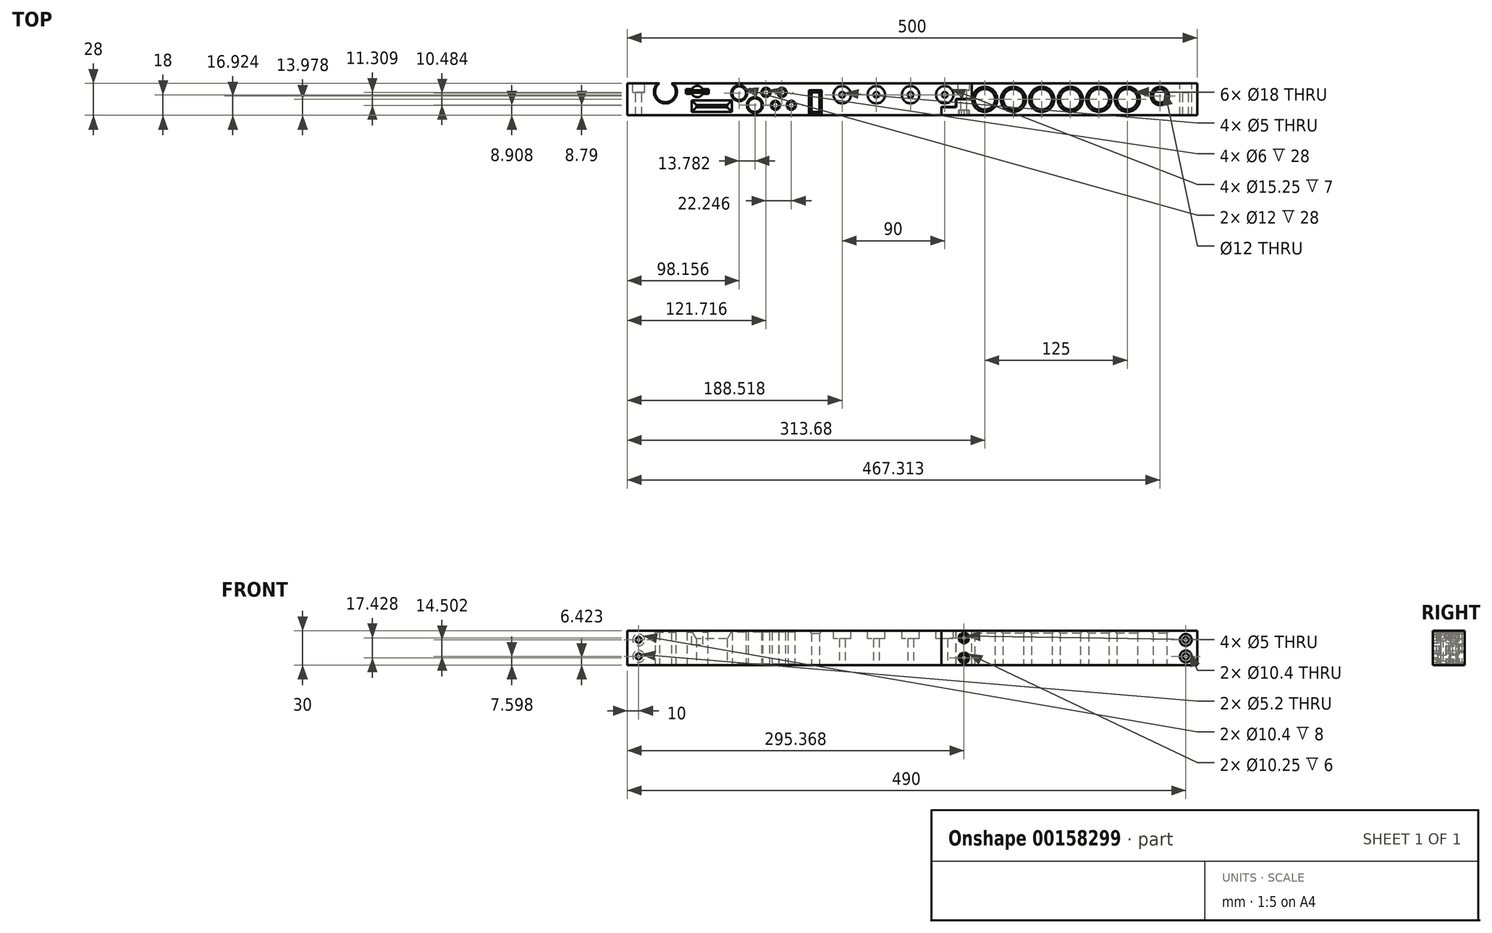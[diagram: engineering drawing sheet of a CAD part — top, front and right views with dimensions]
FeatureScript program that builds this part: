
annotation { "Feature Type Name" : "Feature", "Feature Type Description" : "" }
export const myFeature = defineFeature(function(context is Context, id is Id, definition is map)
    precondition{}
    {
        {
            var Q0;
            Q0=qCreatedBy(makeId("Top.planeOp"),FACE);
            var sketch = newSketch(context, id + "F0", { "sketchPlane" : qUnion([Q0])});
            skLineSegment(sketch, "E0.bottom", {"start": v(0, 0) * mm, "end": v(-211.32, 0) * mm});
            skLineSegment(sketch, "E0.top", {"start": v(0, -28) * mm, "end": v(-250, -28) * mm});
            skLineSegment(sketch, "E0.right", {"start": v(-250, 0) * mm, "end": v(-250, -28) * mm});
            skLineSegment(sketch, "E1.MirrorCS", {"start": v(0, 0) * mm, "end": v(250, 0) * mm});
            skLineSegment(sketch, "E2.MirrorCS", {"start": v(250, 0) * mm, "end": v(250, -28) * mm});
            skLineSegment(sketch, "E3.MirrorCS", {"start": v(0, -28) * mm, "end": v(250, -28) * mm});
            skArc(sketch, "E4", {"start": v(-221.74, 0) * mm, "mid": v(-216.53, -16.56) * mm, "end": v(-211.32, 0) * mm});
            skPoint(sketch, "E5", {"position": v(-211.32, 0) * mm});
            skPoint(sketch, "E6", {"position": v(-221.74, 0) * mm});
            skLineSegment(sketch, "E7.trimOffspring", {"start": v(-221.74, 0) * mm, "end": v(-250, 0) * mm});
            skLineSegment(sketch, "E8.bottom", {"start": v(-189.32, -19) * mm, "end": v(-162.32, -19) * mm});
            skLineSegment(sketch, "E8.top", {"start": v(-189.32, -21) * mm, "end": v(-162.32, -21) * mm});
            skLineSegment(sketch, "E8.left", {"start": v(-189.32, -19) * mm, "end": v(-189.32, -21) * mm});
            skLineSegment(sketch, "E8.right", {"start": v(-162.32, -19) * mm, "end": v(-162.32, -21) * mm});
            skLineSegment(sketch, "E9.bottom", {"start": v(-197.6, -6.14) * mm, "end": v(-179.6, -6.14) * mm});
            skLineSegment(sketch, "E9.top", {"start": v(-197.6, -8.14) * mm, "end": v(-179.6, -8.14) * mm});
            skLineSegment(sketch, "E9.left", {"start": v(-197.6, -6.14) * mm, "end": v(-197.6, -8.14) * mm});
            skLineSegment(sketch, "E9.right", {"start": v(-179.6, -6.14) * mm, "end": v(-179.6, -8.14) * mm});
            skLineSegment(sketch, "E10", {"start": v(-197.6, -7.14) * mm, "end": v(-179.6, -7.14) * mm, "construction": true});
            skLineSegment(sketch, "E11", {"start": v(-188.6, -6.14) * mm, "end": v(-188.6, -8.14) * mm, "construction": true});
            skCircle(sketch, "E12", {"center": v(-151.84, -8.6) * mm, "radius": 6 * mm});
            skCircle(sketch, "E13", {"center": v(-138.06, -19.1) * mm, "radius": 6 * mm});
            skCircle(sketch, "E14", {"center": v(-128.28, -7.9) * mm, "radius": 3 * mm});
            skCircle(sketch, "E15", {"center": v(-120.04, -19.21) * mm, "radius": 3 * mm});
            skCircle(sketch, "E16", {"center": v(-114.28, -7.9) * mm, "radius": 3 * mm});
            skCircle(sketch, "E17", {"center": v(-106.04, -19.21) * mm, "radius": 3 * mm});
            skLineSegment(sketch, "E18", {"start": v(-94.24, -10) * mm, "end": v(-13.08, -10) * mm, "construction": true});
            skCircle(sketch, "E19", {"center": v(-61.48, -10) * mm, "radius": 2.5 * mm});
            skCircle(sketch, "E20.1.0.0", {"center": v(-31.48, -10) * mm, "radius": 2.5 * mm});
            skCircle(sketch, "E20.2.0.0", {"center": v(-1.48, -10) * mm, "radius": 2.5 * mm});
            skCircle(sketch, "E20.3.0.0", {"center": v(28.52, -10) * mm, "radius": 2.5 * mm});
            skLineSegment(sketch, "E20.direction1", {"start": v(-61.48, -10) * mm, "end": v(-31.48, -10) * mm, "construction": true});
            skLineSegment(sketch, "E21.bottom", {"start": v(-81.48, -25) * mm, "end": v(-88.48, -25) * mm});
            skLineSegment(sketch, "E21.top", {"start": v(-81.48, -8) * mm, "end": v(-88.48, -8) * mm});
            skLineSegment(sketch, "E21.left", {"start": v(-81.48, -25) * mm, "end": v(-81.48, -8) * mm});
            skLineSegment(sketch, "E21.right", {"start": v(-88.48, -25) * mm, "end": v(-88.48, -8) * mm});
            skLineSegment(sketch, "E22.bottom", {"start": v(-61.48, -10) * mm, "end": v(-60.58, -10) * mm});
            skLineSegment(sketch, "E22.top", {"start": v(-61.48, -10) * mm, "end": v(-60.58, -10) * mm});
            skLineSegment(sketch, "E22.left", {"start": v(-61.48, -10) * mm, "end": v(-61.48, -10) * mm});
            skLineSegment(sketch, "E22.right", {"start": v(-60.58, -10) * mm, "end": v(-60.58, -10) * mm});
            skCircle(sketch, "E23", {"center": v(63.68, -14.02) * mm, "radius": 9 * mm});
            skCircle(sketch, "E24.1.0.0", {"center": v(88.68, -14.02) * mm, "radius": 9 * mm});
            skCircle(sketch, "E24.2.0.0", {"center": v(113.68, -14.02) * mm, "radius": 9 * mm});
            skCircle(sketch, "E24.3.0.0", {"center": v(138.68, -14.02) * mm, "radius": 9 * mm});
            skCircle(sketch, "E24.4.0.0", {"center": v(163.68, -14.02) * mm, "radius": 9 * mm});
            skCircle(sketch, "E24.5.0.0", {"center": v(188.68, -14.02) * mm, "radius": 9 * mm});
            skLineSegment(sketch, "E24.direction1", {"start": v(63.68, -14.02) * mm, "end": v(88.68, -14.02) * mm, "construction": true});
            skLineSegment(sketch, "E25.bottom", {"start": v(250, -6.13) * mm, "end": v(230, -6.13) * mm, "construction": true});
            skLineSegment(sketch, "E25.top", {"start": v(250, -18.38) * mm, "end": v(230, -18.38) * mm, "construction": true});
            skLineSegment(sketch, "E25.left", {"start": v(250, -6.13) * mm, "end": v(250, -18.38) * mm, "construction": true});
            skLineSegment(sketch, "E25.right", {"start": v(230, -6.13) * mm, "end": v(230, -18.38) * mm, "construction": true});
            skCircle(sketch, "E26", {"center": v(217.31, -11.08) * mm, "radius": 6 * mm});
            skSolve(sketch);
        }
        {
            var Q0;
            Q0 = qSketchRegion(id + "F0", true);
            extrude(context, id + "F1", {"entities" : qUnion([Q0]), "depth" : 30 * mm, "offsetDistance" : 25 * mm});
        }
        {
            var Q0;
            Q0=makeQuery(id+"F1.opExtrude","SWEPT_FACE",FACE,{"disambiguationData":[OSD([sQuery(id+"F0.wireOp",EDGE,"E0.bottom"),sQuery(id+"F0.wireOp",EDGE,"E1.MirrorCS")])]});
            var sketch = newSketch(context, id + "F2", { "sketchPlane" : qUnion([Q0])});
            skLineSegment(sketch, "E27", {"start": v(240, 30) * mm, "end": v(240, 0) * mm, "construction": true});
            skCircle(sketch, "E28", {"center": v(240, 22.1) * mm, "radius": 2.6 * mm});
            skCircle(sketch, "E29", {"center": v(240, 7.6) * mm, "radius": 2.6 * mm});
            skCircle(sketch, "E30", {"center": v(240, 22.1) * mm, "radius": 5.2 * mm});
            skCircle(sketch, "E31", {"center": v(240, 7.6) * mm, "radius": 5.2 * mm});
            skCircle(sketch, "E32.MirrorC", {"center": v(-240, 7.6) * mm, "radius": 2.6 * mm});
            skCircle(sketch, "E33.MirrorC", {"center": v(-240, 22.1) * mm, "radius": 2.6 * mm});
            skCircle(sketch, "E34.MirrorC", {"center": v(-240, 22.1) * mm, "radius": 5.2 * mm});
            skCircle(sketch, "E35.MirrorC", {"center": v(-240, 7.6) * mm, "radius": 5.2 * mm});
            skSolve(sketch);
        }
        {
            var Q0;
            Q0=makeQuery(id+"F2.imprint","IMPRINT",FACE,{"disambiguationData":[TD([[makeQuery(id+"F2.imprint","IMPRINT",EDGE,{"derivedFrom":sQuery(id+"F2.wireOp",EDGE,"E28")}),1.0]])]});
            var Q1;
            Q1=makeQuery(id+"F2.imprint","IMPRINT",FACE,{"disambiguationData":[TD([[makeQuery(id+"F2.imprint","IMPRINT",EDGE,{"derivedFrom":sQuery(id+"F2.wireOp",EDGE,"E29")}),1.0]])]});
            var Q2;
            Q2=makeQuery(id+"F2.imprint","IMPRINT",FACE,{"disambiguationData":[TD([[makeQuery(id+"F2.imprint","IMPRINT",EDGE,{"derivedFrom":sQuery(id+"F2.wireOp",EDGE,"E32.MirrorC")}),-1.0]])]});
            var Q3;
            Q3=makeQuery(id+"F2.imprint","IMPRINT",FACE,{"disambiguationData":[TD([[makeQuery(id+"F2.imprint","IMPRINT",EDGE,{"derivedFrom":sQuery(id+"F2.wireOp",EDGE,"E33.MirrorC")}),-1.0]])]});
            extrude(context, id + "F3", {"entities" : qUnion([Q0, Q1, Q2, Q3]), "operationType" : NewBodyOperationType.REMOVE, "endBound" : BoundingType.THROUGH_ALL, "oppositeDirection" : true, "depth" : 25 * mm, "offsetDistance" : 25 * mm});
        }
        {
            var Q0;
            Q0=makeQuery(id+"F2.imprint","IMPRINT",FACE,{"disambiguationData":[TD([[makeQuery(id+"F2.imprint","IMPRINT",EDGE,{"derivedFrom":sQuery(id+"F2.wireOp",EDGE,"E33.MirrorC")}),1.0]])]});
            var Q1;
            Q1=makeQuery(id+"F2.imprint","IMPRINT",FACE,{"disambiguationData":[TD([[makeQuery(id+"F2.imprint","IMPRINT",EDGE,{"derivedFrom":sQuery(id+"F2.wireOp",EDGE,"E32.MirrorC")}),1.0]])]});
            var Q2;
            Q2=makeQuery(id+"F2.imprint","IMPRINT",FACE,{"disambiguationData":[TD([[makeQuery(id+"F2.imprint","IMPRINT",EDGE,{"derivedFrom":sQuery(id+"F2.wireOp",EDGE,"E29")}),-1.0]])]});
            var Q3;
            Q3=makeQuery(id+"F2.imprint","IMPRINT",FACE,{"disambiguationData":[TD([[makeQuery(id+"F2.imprint","IMPRINT",EDGE,{"derivedFrom":sQuery(id+"F2.wireOp",EDGE,"E28")}),-1.0]])]});
            extrude(context, id + "F4", {"entities" : qUnion([Q0, Q1, Q2, Q3]), "operationType" : NewBodyOperationType.REMOVE, "oppositeDirection" : true, "depth" : 8 * mm, "offsetDistance" : 25 * mm});
        }
        {
            var Q0;
            Q0=makeQuery(id+"F1.opExtrude","CAP_FACE",FACE,{"disambiguationData":[OSD([sQuery(id+"F0.wireOp",EDGE,"E0.bottom"),sQuery(id+"F0.wireOp",EDGE,"E0.top"),sQuery(id+"F0.wireOp",EDGE,"E0.right"),sQuery(id+"F0.wireOp",EDGE,"E1.MirrorCS"),sQuery(id+"F0.wireOp",EDGE,"E2.MirrorCS"),sQuery(id+"F0.wireOp",EDGE,"E3.MirrorCS"),sQuery(id+"F0.wireOp",EDGE,"E4"),sQuery(id+"F0.wireOp",EDGE,"E7.trimOffspring"),sQuery(id+"F0.wireOp",EDGE,"E8.bottom"),sQuery(id+"F0.wireOp",EDGE,"E8.top"),sQuery(id+"F0.wireOp",EDGE,"E8.left"),sQuery(id+"F0.wireOp",EDGE,"E8.right"),sQuery(id+"F0.wireOp",EDGE,"E9.bottom"),sQuery(id+"F0.wireOp",EDGE,"E9.top"),sQuery(id+"F0.wireOp",EDGE,"E9.left"),sQuery(id+"F0.wireOp",EDGE,"E9.right"),sQuery(id+"F0.wireOp",EDGE,"E12"),sQuery(id+"F0.wireOp",EDGE,"E13"),sQuery(id+"F0.wireOp",EDGE,"E14"),sQuery(id+"F0.wireOp",EDGE,"E15"),sQuery(id+"F0.wireOp",EDGE,"E16"),sQuery(id+"F0.wireOp",EDGE,"E17"),sQuery(id+"F0.wireOp",EDGE,"E19"),sQuery(id+"F0.wireOp",EDGE,"E20.1.0.0"),sQuery(id+"F0.wireOp",EDGE,"E20.2.0.0"),sQuery(id+"F0.wireOp",EDGE,"E20.3.0.0"),sQuery(id+"F0.wireOp",EDGE,"E21.bottom"),sQuery(id+"F0.wireOp",EDGE,"E21.top"),sQuery(id+"F0.wireOp",EDGE,"E21.left"),sQuery(id+"F0.wireOp",EDGE,"E21.right"),sQuery(id+"F0.wireOp",EDGE,"E23"),sQuery(id+"F0.wireOp",EDGE,"E24.1.0.0"),sQuery(id+"F0.wireOp",EDGE,"E24.2.0.0"),sQuery(id+"F0.wireOp",EDGE,"E24.3.0.0"),sQuery(id+"F0.wireOp",EDGE,"E24.4.0.0"),sQuery(id+"F0.wireOp",EDGE,"E24.5.0.0"),sQuery(id+"F0.wireOp",EDGE,"E26")])],"isStart":false});
            var sketch = newSketch(context, id + "F5", { "sketchPlane" : qUnion([Q0])});
            skLineSegment(sketch, "E36.0", {"start": v(-188.6, -6.14) * mm, "end": v(-188.6, -8.14) * mm, "construction": true});
            skLineSegment(sketch, "E37.1", {"start": v(-197.6, -7.14) * mm, "end": v(-179.6, -7.14) * mm, "construction": true});
            skCircle(sketch, "E38", {"center": v(-188.6, -7.14) * mm, "radius": 5 * mm});
            skCircle(sketch, "E39", {"center": v(-61.48, -10) * mm, "radius": 7.62 * mm});
            skCircle(sketch, "E40", {"center": v(-31.48, -10) * mm, "radius": 7.62 * mm});
            skCircle(sketch, "E41", {"center": v(-1.48, -10) * mm, "radius": 7.62 * mm});
            skCircle(sketch, "E42", {"center": v(28.52, -10) * mm, "radius": 7.62 * mm});
            skSolve(sketch);
        }
        {
            var Q0;
            {var subQ0=sQuery(id+"F5.wireOp",EDGE,"E38");var subQ1=makeQuery(id+"F1.opExtrude","CAP_EDGE",EDGE,{"disambiguationData":[OSD([sQuery(id+"F0.wireOp",EDGE,"E9.bottom")])],"isStart":false});var subQ2=makeQuery(id+"F5.imprint","INTERSECT",VERTEX,{"disambiguationData":[OD(0.0)],"derivedFrom":[subQ1,subQ0]});Q0=makeQuery(id+"F5.imprint","IMPRINT",FACE,{"disambiguationData":[TD([[makeQuery(id+"F5.imprint","IMPRINT",EDGE,{"disambiguationData":[TD([[subQ2,1.0]])],"derivedFrom":subQ0}),1.0]])]});}
            var Q1;
            {var subQ0=sQuery(id+"F5.wireOp",EDGE,"E38");var subQ1=makeQuery(id+"F1.opExtrude","CAP_EDGE",EDGE,{"disambiguationData":[OSD([sQuery(id+"F0.wireOp",EDGE,"E9.top")])],"isStart":false});var subQ2=makeQuery(id+"F5.imprint","INTERSECT",VERTEX,{"disambiguationData":[OD(0.0)],"derivedFrom":[subQ1,subQ0]});Q1=makeQuery(id+"F5.imprint","IMPRINT",FACE,{"disambiguationData":[TD([[makeQuery(id+"F5.imprint","IMPRINT",EDGE,{"disambiguationData":[TD([[subQ2,-1.0]])],"derivedFrom":subQ0}),1.0]])]});}
            extrude(context, id + "F6", {"entities" : qUnion([Q0, Q1]), "operationType" : NewBodyOperationType.REMOVE, "oppositeDirection" : true, "depth" : 12 * mm, "offsetDistance" : 25 * mm});
        }
        {
            var Q0;
            Q0=makeQuery(id+"F5.imprint","IMPRINT",FACE,{"disambiguationData":[TD([[makeQuery(id+"F5.imprint","IMPRINT",EDGE,{"derivedFrom":sQuery(id+"F5.wireOp",EDGE,"E39")}),1.0]])]});
            var Q1;
            Q1=makeQuery(id+"F5.imprint","IMPRINT",FACE,{"disambiguationData":[TD([[makeQuery(id+"F5.imprint","IMPRINT",EDGE,{"derivedFrom":sQuery(id+"F5.wireOp",EDGE,"E40")}),1.0]])]});
            var Q2;
            Q2=makeQuery(id+"F5.imprint","IMPRINT",FACE,{"disambiguationData":[TD([[makeQuery(id+"F5.imprint","IMPRINT",EDGE,{"derivedFrom":sQuery(id+"F5.wireOp",EDGE,"E41")}),1.0]])]});
            var Q3;
            Q3=makeQuery(id+"F5.imprint","IMPRINT",FACE,{"disambiguationData":[TD([[makeQuery(id+"F5.imprint","IMPRINT",EDGE,{"derivedFrom":sQuery(id+"F5.wireOp",EDGE,"E42")}),1.0]])]});
            extrude(context, id + "F7", {"entities" : qUnion([Q0, Q1, Q2, Q3]), "operationType" : NewBodyOperationType.REMOVE, "oppositeDirection" : true, "depth" : 7 * mm, "offsetDistance" : 25 * mm});
        }
        {
            var Q0;
            Q0=makeQuery(id+"F1.opExtrude","CAP_EDGE",EDGE,{"disambiguationData":[OSD([sQuery(id+"F0.wireOp",EDGE,"E23")])],"isStart":false});
            var Q1;
            Q1=makeQuery(id+"F1.opExtrude","CAP_EDGE",EDGE,{"disambiguationData":[OSD([sQuery(id+"F0.wireOp",EDGE,"E24.1.0.0")])],"isStart":false});
            var Q2;
            Q2=makeQuery(id+"F1.opExtrude","CAP_EDGE",EDGE,{"disambiguationData":[OSD([sQuery(id+"F0.wireOp",EDGE,"E24.2.0.0")])],"isStart":false});
            var Q3;
            Q3=makeQuery(id+"F1.opExtrude","CAP_EDGE",EDGE,{"disambiguationData":[OSD([sQuery(id+"F0.wireOp",EDGE,"E24.3.0.0")])],"isStart":false});
            var Q4;
            Q4=makeQuery(id+"F1.opExtrude","CAP_EDGE",EDGE,{"disambiguationData":[OSD([sQuery(id+"F0.wireOp",EDGE,"E24.4.0.0")])],"isStart":false});
            var Q5;
            Q5=makeQuery(id+"F1.opExtrude","CAP_EDGE",EDGE,{"disambiguationData":[OSD([sQuery(id+"F0.wireOp",EDGE,"E24.5.0.0")])],"isStart":false});
            var Q6;
            Q6=makeQuery(id+"F1.opExtrude","CAP_EDGE",EDGE,{"disambiguationData":[OSD([sQuery(id+"F0.wireOp",EDGE,"E26")])],"isStart":false});
            var Q7;
            Q7=makeQuery(id+"F1.opExtrude","CAP_EDGE",EDGE,{"disambiguationData":[OSD([sQuery(id+"F0.wireOp",EDGE,"E21.left")])],"isStart":false});
            var Q8;
            Q8=makeQuery(id+"F1.opExtrude","CAP_EDGE",EDGE,{"disambiguationData":[OSD([sQuery(id+"F0.wireOp",EDGE,"E21.bottom")])],"isStart":false});
            var Q9;
            Q9=makeQuery(id+"F1.opExtrude","CAP_EDGE",EDGE,{"disambiguationData":[OSD([sQuery(id+"F0.wireOp",EDGE,"E21.right")])],"isStart":false});
            var Q10;
            Q10=makeQuery(id+"F1.opExtrude","CAP_EDGE",EDGE,{"disambiguationData":[OSD([sQuery(id+"F0.wireOp",EDGE,"E21.top")])],"isStart":false});
            chamfer(context, id + "F8", {"entities" : qUnion([Q0, Q1, Q2, Q3, Q4, Q5, Q6, Q7, Q8, Q9, Q10]), "width" : 2 * mm, "tangentPropagation" : true});
        }
        {
            var Q0;
            Q0=makeQuery(id+"F1.opExtrude","CAP_EDGE",EDGE,{"disambiguationData":[OSD([sQuery(id+"F0.wireOp",EDGE,"E17")])],"isStart":false});
            var Q1;
            Q1=makeQuery(id+"F1.opExtrude","CAP_EDGE",EDGE,{"disambiguationData":[OSD([sQuery(id+"F0.wireOp",EDGE,"E15")])],"isStart":false});
            var Q2;
            Q2=makeQuery(id+"F1.opExtrude","CAP_EDGE",EDGE,{"disambiguationData":[OSD([sQuery(id+"F0.wireOp",EDGE,"E16")])],"isStart":false});
            var Q3;
            Q3=makeQuery(id+"F1.opExtrude","CAP_EDGE",EDGE,{"disambiguationData":[OSD([sQuery(id+"F0.wireOp",EDGE,"E14")])],"isStart":false});
            var Q4;
            Q4=makeQuery(id+"F1.opExtrude","CAP_EDGE",EDGE,{"disambiguationData":[OSD([sQuery(id+"F0.wireOp",EDGE,"E13")])],"isStart":false});
            var Q5;
            Q5=makeQuery(id+"F1.opExtrude","CAP_EDGE",EDGE,{"disambiguationData":[OSD([sQuery(id+"F0.wireOp",EDGE,"E12")])],"isStart":false});
            var Q6;
            {var subQ0=sQuery(id+"F5.wireOp",EDGE,"E38");var subQ1=makeQuery(id+"F1.opExtrude","CAP_EDGE",EDGE,{"disambiguationData":[OSD([sQuery(id+"F0.wireOp",EDGE,"E9.top")])],"isStart":false});Q6=makeQuery(id+"F6.boolean.opBoolean","COPY",EDGE,{"derivedFrom":makeQuery(id+"F6.opExtrude","CAP_EDGE",EDGE,{"disambiguationData":[OSD([subQ0]),TDD([makeQuery(id+"F5.imprint","IMPRINT",EDGE,{"disambiguationData":[TD([[makeQuery(id+"F5.imprint","INTERSECT",VERTEX,{"disambiguationData":[OD(0.0)],"derivedFrom":[subQ1,subQ0]}),-1.0]])],"derivedFrom":subQ0})])],"isStart":true})});}
            var Q7;
            {var subQ0=sQuery(id+"F5.wireOp",EDGE,"E38");var subQ1=makeQuery(id+"F1.opExtrude","CAP_EDGE",EDGE,{"disambiguationData":[OSD([sQuery(id+"F0.wireOp",EDGE,"E9.bottom")])],"isStart":false});Q7=makeQuery(id+"F6.boolean.opBoolean","COPY",EDGE,{"derivedFrom":makeQuery(id+"F6.opExtrude","CAP_EDGE",EDGE,{"disambiguationData":[OSD([subQ0]),TDD([makeQuery(id+"F5.imprint","IMPRINT",EDGE,{"disambiguationData":[TD([[makeQuery(id+"F5.imprint","INTERSECT",VERTEX,{"disambiguationData":[OD(0.0)],"derivedFrom":[subQ1,subQ0]}),1.0]])],"derivedFrom":subQ0})])],"isStart":true})});}
            var Q8;
            {var subQ0=sQuery(id+"F0.wireOp",EDGE,"E9.right");var subQ1=sQuery(id+"F0.wireOp",EDGE,"E9.bottom");var subQ3=makeQuery(id+"F1.opExtrude","CAP_EDGE",EDGE,{"disambiguationData":[OSD([subQ1])],"isStart":false});Q8=makeQuery(id+"F6.boolean.opBoolean","SPLIT",EDGE,{"disambiguationData":[TD([makeQuery(id+"F1.opExtrude","SWEPT_FACE",FACE,{"disambiguationData":[OSD([subQ0])]})])],"derivedFrom":subQ3});}
            var Q9;
            Q9=makeQuery(id+"F1.opExtrude","CAP_EDGE",EDGE,{"disambiguationData":[OSD([sQuery(id+"F0.wireOp",EDGE,"E9.right")])],"isStart":false});
            var Q10;
            {var subQ0=sQuery(id+"F0.wireOp",EDGE,"E9.right");var subQ1=sQuery(id+"F0.wireOp",EDGE,"E9.top");var subQ3=makeQuery(id+"F1.opExtrude","CAP_EDGE",EDGE,{"disambiguationData":[OSD([subQ1])],"isStart":false});Q10=makeQuery(id+"F6.boolean.opBoolean","SPLIT",EDGE,{"disambiguationData":[TD([makeQuery(id+"F1.opExtrude","SWEPT_FACE",FACE,{"disambiguationData":[OSD([subQ0])]})])],"derivedFrom":subQ3});}
            var Q11;
            {var subQ0=sQuery(id+"F0.wireOp",EDGE,"E9.left");var subQ1=sQuery(id+"F0.wireOp",EDGE,"E9.top");var subQ3=makeQuery(id+"F1.opExtrude","CAP_EDGE",EDGE,{"disambiguationData":[OSD([subQ1])],"isStart":false});Q11=makeQuery(id+"F6.boolean.opBoolean","SPLIT",EDGE,{"disambiguationData":[TD([makeQuery(id+"F1.opExtrude","SWEPT_FACE",FACE,{"disambiguationData":[OSD([subQ0])]})])],"derivedFrom":subQ3});}
            var Q12;
            Q12=makeQuery(id+"F1.opExtrude","CAP_EDGE",EDGE,{"disambiguationData":[OSD([sQuery(id+"F0.wireOp",EDGE,"E9.left")])],"isStart":false});
            var Q13;
            {var subQ0=sQuery(id+"F0.wireOp",EDGE,"E9.left");var subQ1=sQuery(id+"F0.wireOp",EDGE,"E9.bottom");var subQ3=makeQuery(id+"F1.opExtrude","CAP_EDGE",EDGE,{"disambiguationData":[OSD([subQ1])],"isStart":false});Q13=makeQuery(id+"F6.boolean.opBoolean","SPLIT",EDGE,{"disambiguationData":[TD([makeQuery(id+"F1.opExtrude","SWEPT_FACE",FACE,{"disambiguationData":[OSD([subQ0])]})])],"derivedFrom":subQ3});}
            var Q14;
            Q14=makeQuery(id+"F1.opExtrude","CAP_EDGE",EDGE,{"disambiguationData":[OSD([sQuery(id+"F0.wireOp",EDGE,"E4")])],"isStart":false});
            chamfer(context, id + "F9", {"entities" : qUnion([Q0, Q1, Q2, Q3, Q4, Q5, Q6, Q7, Q8, Q9, Q10, Q11, Q12, Q13, Q14]), "width" : 1 * mm, "tangentPropagation" : true});
        }
        {
            var Q0;
            Q0=makeQuery(id+"F1.opExtrude","CAP_EDGE",EDGE,{"disambiguationData":[OSD([sQuery(id+"F0.wireOp",EDGE,"E8.right")])],"isStart":false});
            var Q1;
            Q1=makeQuery(id+"F1.opExtrude","CAP_EDGE",EDGE,{"disambiguationData":[OSD([sQuery(id+"F0.wireOp",EDGE,"E8.top")])],"isStart":false});
            var Q2;
            Q2=makeQuery(id+"F1.opExtrude","CAP_EDGE",EDGE,{"disambiguationData":[OSD([sQuery(id+"F0.wireOp",EDGE,"E8.left")])],"isStart":false});
            var Q3;
            Q3=makeQuery(id+"F1.opExtrude","CAP_EDGE",EDGE,{"disambiguationData":[OSD([sQuery(id+"F0.wireOp",EDGE,"E8.bottom")])],"isStart":false});
            chamfer(context, id + "F10", {"entities" : qUnion([Q0, Q1, Q2, Q3]), "chamferType" : ChamferType.OFFSET_ANGLE, "width" : 7 * mm, "oppositeDirection" : true, "angle" : 30 * degree, "tangentPropagation" : true});
        }
        {
            var Q0;
            Q0=makeQuery(id+"F5.imprint","IMPRINT",FACE,{"disambiguationData":[TD([[makeQuery(id+"F5.imprint","IMPRINT",EDGE,{"derivedFrom":sQuery(id+"F5.wireOp",EDGE,"E39")}),-1.0]])]});
            var sketch = newSketch(context, id + "F11", { "sketchPlane" : qUnion([Q0])});
            skLineSegment(sketch, "E43", {"start": v(52.4, -13.9) * mm, "end": v(38.58, -13.9) * mm});
            skLineSegment(sketch, "E44", {"start": v(38.58, -13.9) * mm, "end": v(38.58, -20.95) * mm});
            skLineSegment(sketch, "E45", {"start": v(38.58, -20.95) * mm, "end": v(25.75, -20.95) * mm});
            skLineSegment(sketch, "E46", {"start": v(25.75, -20.95) * mm, "end": v(25.75, -33.4) * mm});
            skLineSegment(sketch, "E47.0", {"start": v(52.4, 6.43) * mm, "end": v(52.4, -13.9) * mm});
            skLineSegment(sketch, "E48.0", {"start": v(25.55, -20.75) * mm, "end": v(25.55, -33.4) * mm});
            skLineSegment(sketch, "E48.1", {"start": v(52.2, 6.43) * mm, "end": v(52.2, -13.7) * mm});
            skLineSegment(sketch, "E48.2", {"start": v(52.2, -13.7) * mm, "end": v(38.38, -13.7) * mm});
            skLineSegment(sketch, "E48.3", {"start": v(38.38, -13.7) * mm, "end": v(38.38, -20.75) * mm});
            skLineSegment(sketch, "E48.4", {"start": v(38.38, -20.75) * mm, "end": v(25.55, -20.75) * mm});
            skLineSegment(sketch, "E49", {"start": v(52.2, 6.43) * mm, "end": v(52.4, 6.43) * mm});
            skLineSegment(sketch, "E50", {"start": v(25.55, -33.4) * mm, "end": v(25.75, -33.4) * mm});
            skSolve(sketch);
        }
        {
            var Q0;
            Q0 = qSketchRegion(id + "F11", true);
            extrude(context, id + "F12", {"entities" : qUnion([Q0]), "operationType" : NewBodyOperationType.REMOVE, "endBound" : BoundingType.THROUGH_ALL, "oppositeDirection" : true, "depth" : 25 * mm, "offsetDistance" : 25 * mm});
        }
        {
            var Q0;
            Q0=makeQuery(id+"F2.imprint","IMPRINT",FACE,{"disambiguationData":[TD([[makeQuery(id+"F2.imprint","IMPRINT",EDGE,{"derivedFrom":sQuery(id+"F2.wireOp",EDGE,"E34.MirrorC")}),1.0]])]});
            var sketch = newSketch(context, id + "F13", { "sketchPlane" : qUnion([Q0])});
            skCircle(sketch, "E51", {"center": v(-45.37, 23.85) * mm, "radius": 2.5 * mm, "construction": true});
            skCircle(sketch, "E52", {"center": v(-45.37, 6.42) * mm, "radius": 2.5 * mm, "construction": true});
            skCircle(sketch, "E53", {"center": v(-45.37, 23.85) * mm, "radius": 5.12 * mm});
            skCircle(sketch, "E54", {"center": v(-45.37, 6.42) * mm, "radius": 5.12 * mm});
            skSolve(sketch);
        }
        {
            var Q0;
            {var subQ31=sQuery(id+"F0.wireOp",EDGE,"E3.MirrorCS");var subQ32=sQuery(id+"F0.wireOp",EDGE,"E2.MirrorCS");var subQ35=sQuery(id+"F0.wireOp",EDGE,"E0.top");Q0=makeQuery(id+"F12.boolean.opBoolean","SPLIT",FACE,{"disambiguationData":[TD([makeQuery(id+"F1.opExtrude","SWEPT_FACE",FACE,{"disambiguationData":[OSD([subQ32])]})])],"derivedFrom":makeQuery(id+"F1.opExtrude","SWEPT_FACE",FACE,{"disambiguationData":[OSD([subQ35,subQ31])]})});}
            var sketch = newSketch(context, id + "F14", { "sketchPlane" : qUnion([Q0])});
            skCircle(sketch, "E55.0", {"center": v(45.37, 23.85) * mm, "radius": 2.5 * mm, "construction": true});
            skCircle(sketch, "E56.0", {"center": v(45.37, 6.42) * mm, "radius": 2.5 * mm, "construction": true});
            skCircle(sketch, "E57.cCircle", {"center": v(45.37, 23.85) * mm, "radius": 4.15 * mm, "construction": true});
            skLineSegment(sketch, "E57.0", {"start": v(49.52, 26.25) * mm, "end": v(49.52, 21.46) * mm});
            skLineSegment(sketch, "E57.1", {"start": v(49.52, 21.46) * mm, "end": v(45.37, 19.06) * mm});
            skLineSegment(sketch, "E57.2", {"start": v(45.37, 19.06) * mm, "end": v(41.22, 21.46) * mm});
            skLineSegment(sketch, "E57.3", {"start": v(41.22, 21.46) * mm, "end": v(41.22, 26.25) * mm});
            skLineSegment(sketch, "E57.4", {"start": v(41.22, 26.25) * mm, "end": v(45.37, 28.64) * mm});
            skLineSegment(sketch, "E57.5", {"start": v(45.37, 28.64) * mm, "end": v(49.52, 26.25) * mm});
            skPoint(sketch, "E57.0.midPoint", {"position": v(49.52, 23.85) * mm});
            skCircle(sketch, "E58.cCircle", {"center": v(45.37, 6.42) * mm, "radius": 4.15 * mm, "construction": true});
            skLineSegment(sketch, "E58.0", {"start": v(47.8, 10.56) * mm, "end": v(50.16, 6.4) * mm});
            skLineSegment(sketch, "E58.1", {"start": v(50.16, 6.4) * mm, "end": v(47.74, 2.26) * mm});
            skLineSegment(sketch, "E58.2", {"start": v(47.74, 2.26) * mm, "end": v(42.94, 2.29) * mm});
            skLineSegment(sketch, "E58.3", {"start": v(42.94, 2.29) * mm, "end": v(40.58, 6.45) * mm});
            skLineSegment(sketch, "E58.4", {"start": v(40.58, 6.45) * mm, "end": v(43, 10.59) * mm});
            skLineSegment(sketch, "E58.5", {"start": v(43, 10.59) * mm, "end": v(47.8, 10.56) * mm});
            skPoint(sketch, "E58.0.midPoint", {"position": v(48.98, 8.47) * mm});
            skSolve(sketch);
        }
        {
            var Q0;
            Q0 = qSketchRegion(id + "F14", true);
            extrude(context, id + "F15", {"entities" : qUnion([Q0]), "operationType" : NewBodyOperationType.REMOVE, "oppositeDirection" : true, "depth" : 4.5 * mm, "offsetDistance" : 25 * mm});
        }
        {
            var Q0;
            Q0=makeQuery(id+"F2.imprint","IMPRINT",FACE,{"disambiguationData":[TD([[makeQuery(id+"F2.imprint","IMPRINT",EDGE,{"derivedFrom":sQuery(id+"F2.wireOp",EDGE,"E34.MirrorC")}),1.0]])]});
            var sketch = newSketch(context, id + "F16", { "sketchPlane" : qUnion([Q0])});
            skCircle(sketch, "E59.0", {"center": v(-45.37, 23.85) * mm, "radius": 2.5 * mm});
            skCircle(sketch, "E60.0", {"center": v(-45.37, 6.42) * mm, "radius": 2.5 * mm});
            skSolve(sketch);
        }
        {
            var Q0;
            Q0 = qSketchRegion(id + "F16", true);
            extrude(context, id + "F17", {"entities" : qUnion([Q0]), "operationType" : NewBodyOperationType.REMOVE, "endBound" : BoundingType.THROUGH_ALL, "oppositeDirection" : true, "depth" : 25 * mm, "offsetDistance" : 25 * mm});
        }
        {
            var Q0;
            Q0 = qSketchRegion(id + "F13", true);
            extrude(context, id + "F18", {"entities" : qUnion([Q0]), "operationType" : NewBodyOperationType.REMOVE, "oppositeDirection" : true, "depth" : 6 * mm, "offsetDistance" : 25 * mm});
        }
        {
            var Q0;
            Q0=makeQuery(id+"F0.imprint","IMPRINT",FACE,{"disambiguationData":[TD([[makeQuery(id+"F0.imprint","IMPRINT",EDGE,{"derivedFrom":sQuery(id+"F0.wireOp",EDGE,"E0.bottom")}),1.0]])]});
            var sketch = newSketch(context, id + "F19", { "sketchPlane" : qUnion([Q0])});
            skCircle(sketch, "E61.0", {"center": v(-138.06, -19.1) * mm, "radius": 6 * mm});
            skCircle(sketch, "E62.0", {"center": v(-151.84, -8.6) * mm, "radius": 6 * mm});
            skCircle(sketch, "E63.0", {"center": v(-128.28, -7.9) * mm, "radius": 3 * mm});
            skCircle(sketch, "E64.0", {"center": v(-114.28, -7.9) * mm, "radius": 3 * mm});
            skCircle(sketch, "E65.0", {"center": v(-106.04, -19.21) * mm, "radius": 3 * mm});
            skCircle(sketch, "E66.0", {"center": v(-120.04, -19.21) * mm, "radius": 3 * mm});
            skSolve(sketch);
        }
        {
            var Q0;
            Q0 = qSketchRegion(id + "F19", true);
            extrude(context, id + "F20", {"entities" : qUnion([Q0]), "operationType" : NewBodyOperationType.ADD, "depth" : 1 * mm, "offsetDistance" : 25 * mm});
        }
    });
